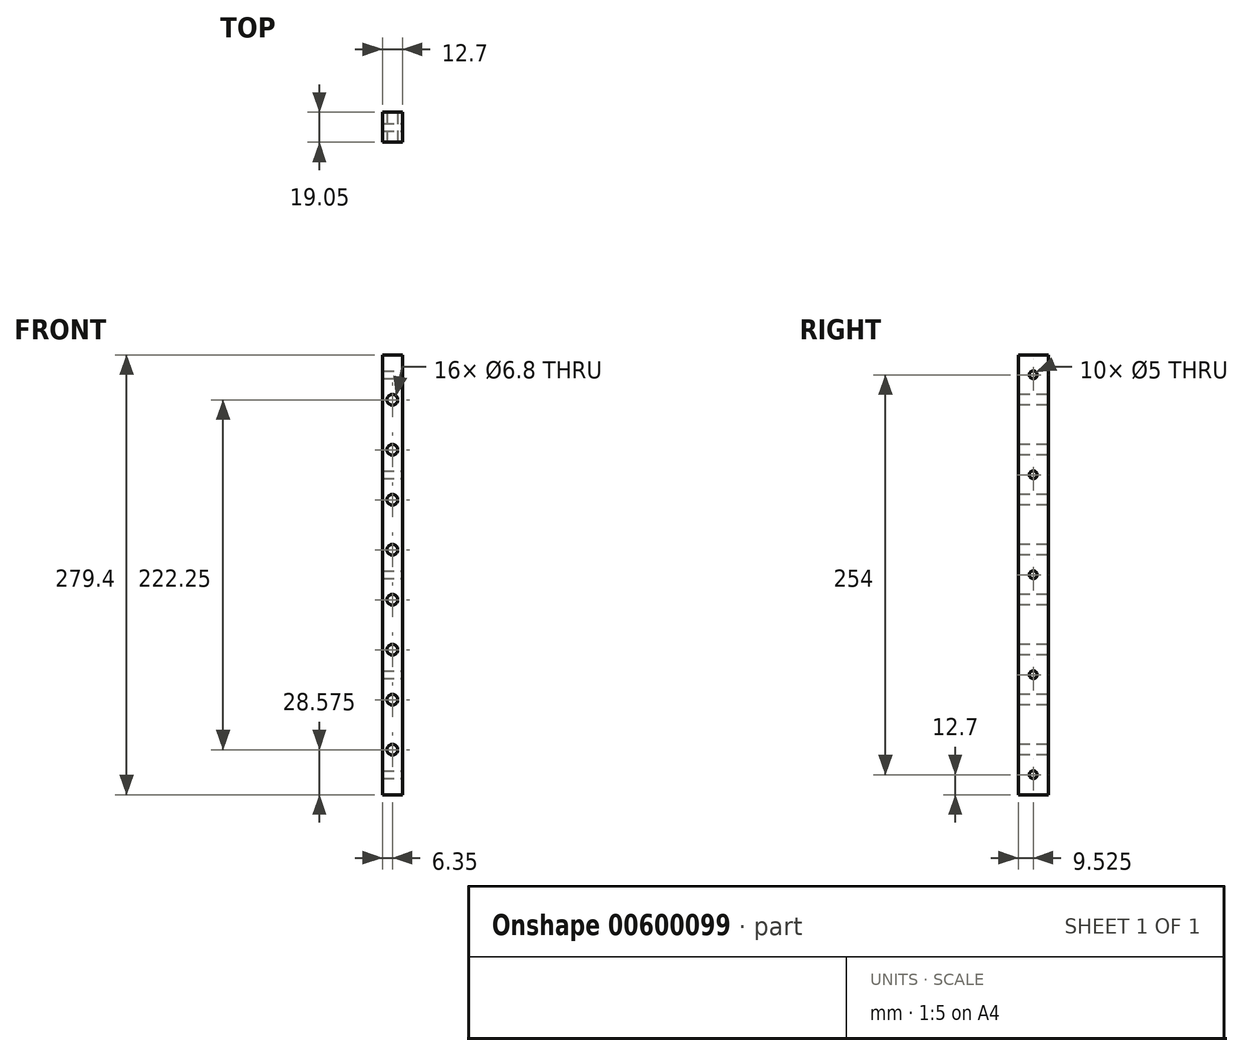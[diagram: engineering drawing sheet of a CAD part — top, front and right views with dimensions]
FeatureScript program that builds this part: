
annotation { "Feature Type Name" : "Feature", "Feature Type Description" : "" }
export const myFeature = defineFeature(function(context is Context, id is Id, definition is map)
    precondition{}
    {
        {
            var Q0;
            Q0=qCreatedBy(makeId("Front.planeOp"),FACE);
            var sketch = newSketch(context, id + "F0", { "sketchPlane" : qUnion([Q0])});
            skLineSegment(sketch, "E0.bottom", {"start": v(6.35, 139.7) * mm, "end": v(-6.35, 139.7) * mm});
            skLineSegment(sketch, "E0.top", {"start": v(6.35, -139.7) * mm, "end": v(-6.35, -139.7) * mm});
            skLineSegment(sketch, "E0.left", {"start": v(6.35, 139.7) * mm, "end": v(6.35, -139.7) * mm});
            skLineSegment(sketch, "E0.right", {"start": v(-6.35, 139.7) * mm, "end": v(-6.35, -139.7) * mm});
            skPoint(sketch, "E0.middle", {"position": v(0, 0) * mm});
            skSolve(sketch);
        }
        {
            var Q0;
            Q0 = qSketchRegion(id + "F0", true);
            extrude(context, id + "F1", {"entities" : qUnion([Q0]), "depth" : 19.05 * mm, "offsetDistance" : 25.4 * mm});
        }
        {
            var Q0;
            Q0=makeQuery(id+"F1.opExtrude","SWEPT_FACE",FACE,{"disambiguationData":[OSD([sQuery(id+"F0.wireOp",EDGE,"E0.left")])]});
            var sketch = newSketch(context, id + "F2", { "sketchPlane" : qUnion([Q0])});
            skLineSegment(sketch, "E1", {"start": v(-9.52, 0) * mm, "end": v(-9.53, 139.7) * mm});
            skPoint(sketch, "E1.startSnap0", {"position": v(-9.53, 139.7) * mm});
            skLineSegment(sketch, "E2", {"start": v(-9.53, 139.7) * mm, "end": v(-9.52, -139.7) * mm});
            skPoint(sketch, "E3", {"position": v(-9.52, 0) * mm});
            skPoint(sketch, "E4", {"position": v(-9.53, 63.5) * mm});
            skPoint(sketch, "E5", {"position": v(-9.53, 127) * mm});
            skPoint(sketch, "E6", {"position": v(-9.52, -63.5) * mm});
            skPoint(sketch, "E7", {"position": v(-9.52, -127) * mm});
            skSolve(sketch);
        }
        {
            var Q0;
            Q0=sQuery(id+"F2.wireOp",VERTEX,"E5");
            var Q1;
            Q1=sQuery(id+"F2.wireOp",VERTEX,"E4");
            var Q2;
            Q2=sQuery(id+"F2.wireOp",VERTEX,"E3");
            var Q3;
            Q3=sQuery(id+"F2.wireOp",VERTEX,"E6");
            var Q4;
            Q4=sQuery(id+"F2.wireOp",VERTEX,"E7");
            var Q5;
            Q5=makeQuery(id+"F1.opExtrude","SWEPT_BODY",BODY,{"disambiguationData":[OSD([sQuery(id+"F0.wireOp",EDGE,"E0.bottom"),sQuery(id+"F0.wireOp",EDGE,"E0.top"),sQuery(id+"F0.wireOp",EDGE,"E0.left"),sQuery(id+"F0.wireOp",EDGE,"E0.right")])]});
            hole(context, id + "F3", {"style" : HoleStyle.SIMPLE, "endStyle" : HoleEndStyle.THROUGH, "standardTappedOrClearance" : lookupTablePath({ "standard" : "ISO", "engagement" : "75%", "pitch" : "1 mm", "size" : "M6", "type" : "Tapped" }), "standardBlindInLast" : lookupTablePath({ "standard" : "ISO", "engagement" : "75%", "pitch" : "1 mm", "size" : "M6", "type" : "Tapped" }), "holeDiameter" : 5 * mm, "majorDiameter" : 6 * mm, "showTappedDepth" : true, "isTappedThrough" : true, "tappedDepth" : 12.7 * mm, "tapClearance" : 3, "locations" : qUnion([Q0, Q1, Q2, Q3, Q4]), "scope" : qUnion([Q5])});
        }
        {
            var Q0;
            Q0=makeQuery(id+"F1.opExtrude","CAP_FACE",FACE,{"disambiguationData":[OSD([sQuery(id+"F0.wireOp",EDGE,"E0.bottom"),sQuery(id+"F0.wireOp",EDGE,"E0.top"),sQuery(id+"F0.wireOp",EDGE,"E0.left"),sQuery(id+"F0.wireOp",EDGE,"E0.right")])],"isStart":false});
            var sketch = newSketch(context, id + "F4", { "sketchPlane" : qUnion([Q0])});
            skPoint(sketch, "E8", {"position": v(0, 15.88) * mm});
            skPoint(sketch, "E9", {"position": v(0, -15.88) * mm});
            skPoint(sketch, "E10", {"position": v(0, -47.62) * mm});
            skPoint(sketch, "E11", {"position": v(0, -79.38) * mm});
            skPoint(sketch, "E12", {"position": v(0, -111.12) * mm});
            skPoint(sketch, "E13", {"position": v(0, 47.62) * mm});
            skPoint(sketch, "E14", {"position": v(0, 79.38) * mm});
            skPoint(sketch, "E15", {"position": v(0, 111.12) * mm});
            skSolve(sketch);
        }
        {
            var Q0;
            Q0=sQuery(id+"F4.wireOp",VERTEX,"E15");
            var Q1;
            Q1=sQuery(id+"F4.wireOp",VERTEX,"E14");
            var Q2;
            Q2=sQuery(id+"F4.wireOp",VERTEX,"E13");
            var Q3;
            Q3=sQuery(id+"F4.wireOp",VERTEX,"E8");
            var Q4;
            Q4=sQuery(id+"F4.wireOp",VERTEX,"E9");
            var Q5;
            Q5=sQuery(id+"F4.wireOp",VERTEX,"E10");
            var Q6;
            Q6=sQuery(id+"F4.wireOp",VERTEX,"E11");
            var Q7;
            Q7=sQuery(id+"F4.wireOp",VERTEX,"E12");
            var Q8;
            Q8=makeQuery(id+"F1.opExtrude","SWEPT_BODY",BODY,{"disambiguationData":[OSD([sQuery(id+"F0.wireOp",EDGE,"E0.bottom"),sQuery(id+"F0.wireOp",EDGE,"E0.top"),sQuery(id+"F0.wireOp",EDGE,"E0.left"),sQuery(id+"F0.wireOp",EDGE,"E0.right")])]});
            hole(context, id + "F5", {"style" : HoleStyle.SIMPLE, "endStyle" : HoleEndStyle.THROUGH, "standardTappedOrClearance" : lookupTablePath({ "standard" : "ISO", "engagement" : "75%", "pitch" : "1.25 mm", "size" : "M8", "type" : "Tapped" }), "standardBlindInLast" : lookupTablePath({ "standard" : "ISO", "engagement" : "75%", "pitch" : "1.25 mm", "size" : "M8", "type" : "Tapped" }), "holeDiameter" : 6.8 * mm, "majorDiameter" : 8 * mm, "showTappedDepth" : true, "isTappedThrough" : true, "tappedDepth" : 12.7 * mm, "tapClearance" : 3, "locations" : qUnion([Q0, Q1, Q2, Q3, Q4, Q5, Q6, Q7]), "scope" : qUnion([Q8])});
        }
    });
